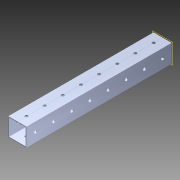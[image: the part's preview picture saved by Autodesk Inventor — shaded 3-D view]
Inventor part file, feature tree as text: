
AUTODESK INVENTOR PART (.ipt)
format: ipt  version: 2014 (Build 180170000, 170)  size: 1,153,024 bytes
history: native  units: in
note: dims shown in document units (in); Inventor stores cm internally (conversion verified against a paired STEP export)
features: pattern_circular x1, other x1, plane x1, extrude x1, imported_body x1, sketch x1
ambient origin geometry x8: Origin, YZ Plane, XZ Plane, XY Plane, X Axis, Y Axis, Z Axis, Center Point
bodies: Body1 (feature_tree)
feature tree (6):
  pattern_circular  "CirPattern2"
  other  "217-3426-STEP1"
  plane  "Work Plane1"
  extrude  "Extrusion1"  Depth=3937.0079in TaperAngle=0.0deg
  imported_body  "Base1"
  sketch  "Sketch1"  dims[d0=-8.0in d1=3937.0079in d2=0.0in]
